# Revit family: Faucet-Two_Handle-American_Standard-Colony_Pro-7075.20X_Series
name_source: partatom
category: Plumbing Fixtures
units: mm (PartAtom-declared; Revit-internal decimal feet)

## family parameters
Always vertical = No
Cut with Voids When Loaded = No
OmniClass Number = 23.45.55.17
OmniClass Title = Mixing Faucets
Part Type = Normal
Room Calculation Point = No
Round Connector Dimension = Use Diameter
Shared = Yes
Work Plane-Based = Yes

## types (9) — shared parameters
ADA Compliant = Yes
CW Connection = Yes
CWFU = 1.5
Cold Water Connection Diameter = 3/8"
Cold Water Connection Radius = 3/16"
Cold Water Connection Width = 2"
Default Elevation = 0"
Drain Depth = 3"
Flow Rate = 1.2 gpm (4.5 L/min.)
HW Connection = Yes
HWFU = 1.5
Height = 4 1/4"
Hot Water Connection Diameter = 0"
Hot Water Connection Radius = 3/16"
Hot Water Connection Width = 2"
Installation Instruction Link = https://americanstandard.box.com
Installation Type = Deck Mounted
Length = 6 3/8"
Manufacturer = American Standard
Price = Prices may vary. Please consult Manufacturer Representative for most up-to-date price list.
Product Documentation Link = https://americanstandard.box.com
Product Page URL = https://www.americanstandard.ca
Revised Date = 02/21/2023
URL = http://www.americanstandard-us.com
Vent Connection = No
WFU = 2
Warranty Information = Limited Lifetime Warranty
Waste Connection = No
Width = 9 3/4"

## per-type parameters (varying)
| type | Description | Finish | Material | Pop-Up Hole & Rod |
| 7075.200.002 | Colony® PRO Two-Handle Centerset Lavatory Faucet with Metal Drain. | Metal-American Standard-002-Polished Chrome | Metal-American Standard-002-Polished Chrome | No |
| 7075.202.002 | Colony® PRO Two-Handle Centerset Lavatory Faucet with 50/50 pop-up drain. | Metal-American Standard-002-Polished Chrome | Metal-American Standard-002-Polished Chrome | Yes |
| 7075.205.002 | Colony® PRO Two-Handle Centerset Lavatory Faucet with pop-up hole, plug button and rod. | Metal-American Standard-002-Polished Chrome | Metal-American Standard-002-Polished Chrome | Yes |
| 7075.200.295 | Colony® PRO Two-Handle Centerset Lavatory Faucet with Metal Drain. | Metal-American Standard-295-Satin Nickel | Metal-American Standard-295-Satin Nickel | No |
| 7075.200.278 | Colony® PRO Two-Handle Centerset Lavatory Faucet with Metal Drain. | Metal-American Standard-278-Legacy Bronze | Metal-American Standard-278-Legacy Bronze | No |
| 7075.202.295 | Colony® PRO Two-Handle Centerset Lavatory Faucet with 50/50 pop-up drain. | Metal-American Standard-295-Satin Nickel | Metal-American Standard-295-Satin Nickel | Yes |
| 7075.202.278 | Colony® PRO Two-Handle Centerset Lavatory Faucet with 50/50 pop-up drain. | Metal-American Standard-278-Legacy Bronze | Metal-American Standard-278-Legacy Bronze | Yes |
| 7075.205.295 | Colony® PRO Two-Handle Centerset Lavatory Faucet with pop-up hole, plug button and rod. | Metal-American Standard-295-Satin Nickel | Metal-American Standard-295-Satin Nickel | Yes |
| 7075.205.278 | Colony® PRO Two-Handle Centerset Lavatory Faucet with pop-up hole, plug button and rod. | Metal-American Standard-278-Legacy Bronze | Metal-American Standard-278-Legacy Bronze | Yes |

note: column(s) folded — value = type name in every type: Model

## geometry (parser evidence)
native form markers: Sweep x2
no freeform markers — native parametric forms only
